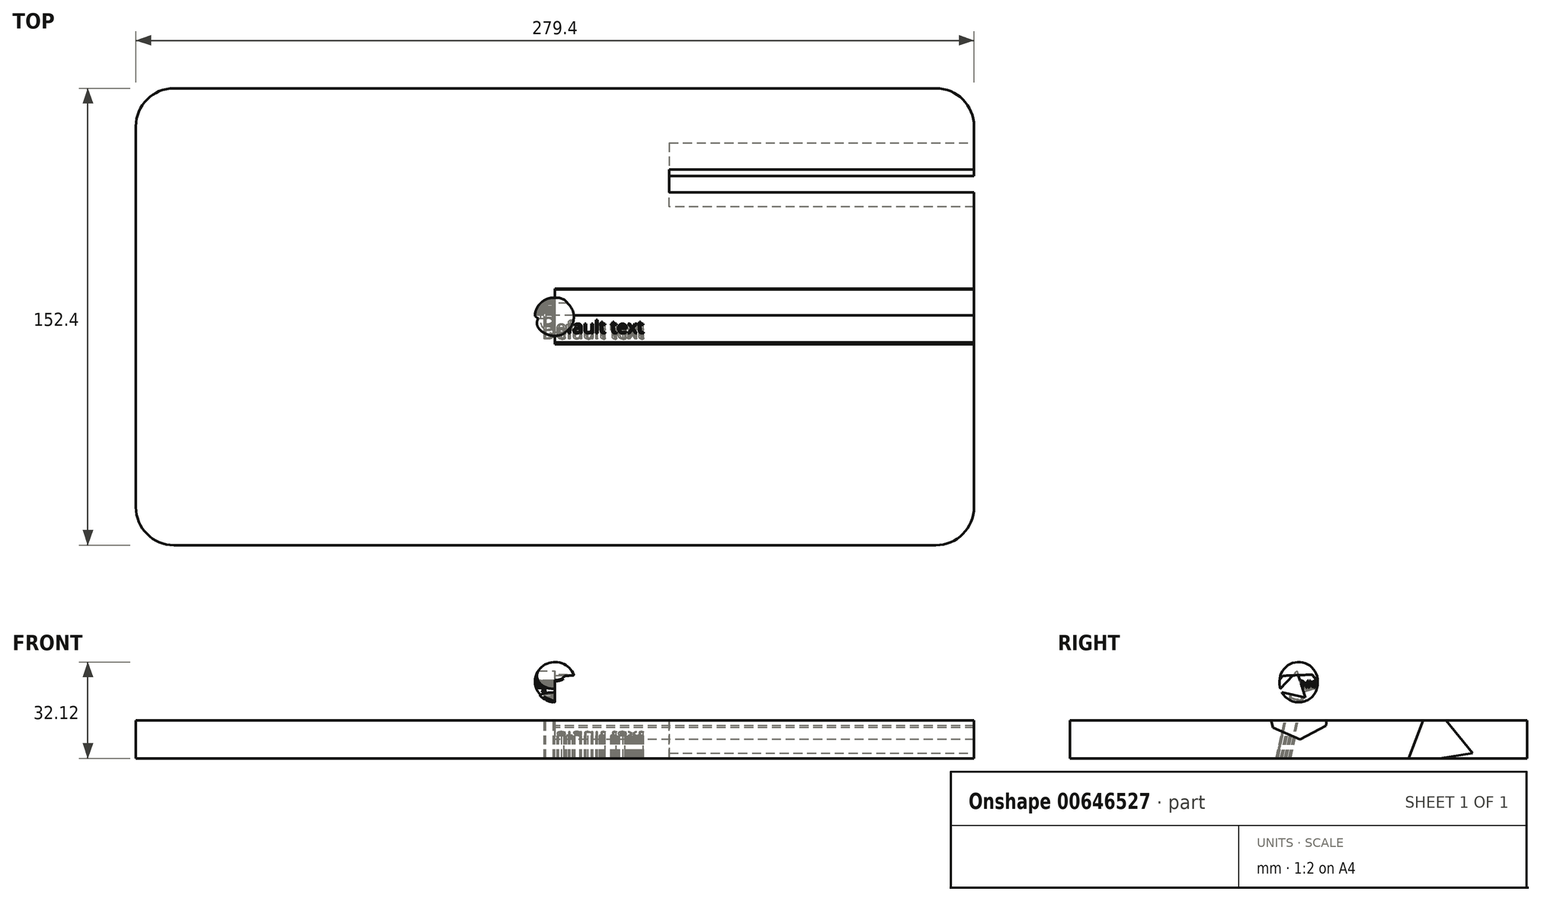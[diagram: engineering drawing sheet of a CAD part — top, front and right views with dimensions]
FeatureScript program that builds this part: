
annotation { "Feature Type Name" : "Feature", "Feature Type Description" : "" }
export const myFeature = defineFeature(function(context is Context, id is Id, definition is map)
    precondition{}
    {
        {
            var Q0;
            Q0=qCreatedBy(makeId("Top.planeOp"),FACE);
            var sketch = newSketch(context, id + "F0", { "sketchPlane" : qUnion([Q0])});
            skLineSegment(sketch, "E0.bottom", {"start": v(139.7, 76.2) * mm, "end": v(-139.7, 76.2) * mm});
            skLineSegment(sketch, "E0.top", {"start": v(139.7, -76.2) * mm, "end": v(-139.7, -76.2) * mm});
            skLineSegment(sketch, "E0.left", {"start": v(139.7, 76.2) * mm, "end": v(139.7, -76.2) * mm});
            skLineSegment(sketch, "E0.right", {"start": v(-139.7, 76.2) * mm, "end": v(-139.7, -76.2) * mm});
            skPoint(sketch, "E0.middle", {"position": v(0, 0) * mm});
            skSolve(sketch);
        }
        {
            var Q0;
            Q0=makeQuery(id+"F0.imprint","IMPRINT",FACE,{"disambiguationData":[TD([[makeQuery(id+"F0.imprint","IMPRINT",EDGE,{"derivedFrom":sQuery(id+"F0.wireOp",EDGE,"E0.bottom")}),1.0]])]});
            extrude(context, id + "F1", {"entities" : qUnion([Q0]), "endBound" : BoundingType.SYMMETRIC, "depth" : 12.7 * mm, "offsetDistance" : 25.4 * mm});
        }
        {
            var Q0;
            Q0=makeQuery(id+"F1.opExtrude","SWEPT_EDGE",EDGE,{"disambiguationData":[OSD([sQuery(id+"F0.wireOp",EDGE,"E0.top"),sQuery(id+"F0.wireOp",EDGE,"E0.right")])]});
            var Q1;
            Q1=makeQuery(id+"F1.opExtrude","SWEPT_EDGE",EDGE,{"disambiguationData":[OSD([sQuery(id+"F0.wireOp",EDGE,"E0.bottom"),sQuery(id+"F0.wireOp",EDGE,"E0.right")])]});
            var Q2;
            Q2=makeQuery(id+"F1.opExtrude","SWEPT_EDGE",EDGE,{"disambiguationData":[OSD([sQuery(id+"F0.wireOp",EDGE,"E0.bottom"),sQuery(id+"F0.wireOp",EDGE,"E0.left")])]});
            var Q3;
            Q3=makeQuery(id+"F1.opExtrude","SWEPT_EDGE",EDGE,{"disambiguationData":[OSD([sQuery(id+"F0.wireOp",EDGE,"E0.top"),sQuery(id+"F0.wireOp",EDGE,"E0.left")])]});
            fillet(context, id + "F2", {"entities" : qUnion([Q0, Q1, Q2, Q3]), "radius" : 12.7 * mm, "tangentPropagation" : true, "allowEdgeOverflow" : false});
        }
        {
            var Q0;
            Q0=makeQuery(id+"F1.opExtrude","CAP_FACE",FACE,{"disambiguationData":[OSD([sQuery(id+"F0.wireOp",EDGE,"E0.bottom"),sQuery(id+"F0.wireOp",EDGE,"E0.top"),sQuery(id+"F0.wireOp",EDGE,"E0.left"),sQuery(id+"F0.wireOp",EDGE,"E0.right")])],"isStart":false});
            var sketch = newSketch(context, id + "F3", { "sketchPlane" : qUnion([Q0])});
            skLineSegment(sketch, "E1", {"start": v(0, 76.2) * mm, "end": v(0, -76.2) * mm, "construction": true});
            skLineSegment(sketch, "E2", {"start": v(-139.7, 0) * mm, "end": v(139.7, 0) * mm, "construction": true});
            skPoint(sketch, "E3", {"position": v(0, 6.35) * mm});
            skPoint(sketch, "E4", {"position": v(0, -6.35) * mm});
            skArc(sketch, "E5", {"start": v(0, -6.35) * mm, "mid": v(6.72, 0) * mm, "end": v(0, 6.35) * mm});
            skLineSegment(sketch, "E6", {"start": v(0, 6.35) * mm, "end": v(0, -6.35) * mm});
            skSolve(sketch);
        }
        {
            var Q0;
            Q0=makeQuery(id+"F3.imprint","IMPRINT",FACE,{"disambiguationData":[TD([[makeQuery(id+"F3.imprint","IMPRINT",EDGE,{"derivedFrom":sQuery(id+"F3.wireOp",EDGE,"E5")}),1.0]])]});
            extrude(context, id + "F4", {"entities" : qUnion([Q0]), "operationType" : NewBodyOperationType.ADD, "depth" : 12.7 * mm, "offsetDistance" : 25.4 * mm});
        }
        {
            var Q0;
            Q0=makeQuery(id+"F4.opExtrude","CAP_FACE",FACE,{"disambiguationData":[OSD([sQuery(id+"F3.wireOp",EDGE,"E5"),sQuery(id+"F3.wireOp",EDGE,"E6")])],"isStart":false});
            var Q1;
            Q1=makeQuery(id+"F4.opExtrude","CAP_EDGE",EDGE,{"disambiguationData":[OSD([sQuery(id+"F3.wireOp",EDGE,"E6")])],"isStart":false});
            revolve(context, id + "F5", {"operationType" : NewBodyOperationType.ADD, "entities" : qUnion([Q0]), "axis" : qUnion([Q1]), "revolveType" : RevolveType.FULL});
        }
        {
            var Q0;
            Q0=makeQuery(id+"F4.opExtrude","SWEPT_FACE",FACE,{"disambiguationData":[OSD([sQuery(id+"F3.wireOp",EDGE,"E6")])]});
            var sketch = newSketch(context, id + "F6", { "sketchPlane" : qUnion([Q0])});
            skCircle(sketch, "E7.cCircle", {"center": v(0, 11.24) * mm, "radius": 10.14 * mm, "construction": true});
            skLineSegment(sketch, "E7.0", {"start": v(11.07, 13.3) * mm, "end": v(8.51, 3.87) * mm});
            skLineSegment(sketch, "E7.1", {"start": v(8.51, 3.87) * mm, "end": v(-0.45, -0.01) * mm});
            skLineSegment(sketch, "E7.2", {"start": v(-0.45, -0.01) * mm, "end": v(-9.08, 4.57) * mm});
            skLineSegment(sketch, "E7.3", {"start": v(-9.08, 4.57) * mm, "end": v(-10.87, 14.18) * mm});
            skLineSegment(sketch, "E7.4", {"start": v(-10.87, 14.18) * mm, "end": v(-4.48, 21.57) * mm});
            skLineSegment(sketch, "E7.5", {"start": v(-4.48, 21.57) * mm, "end": v(5.29, 21.18) * mm});
            skLineSegment(sketch, "E7.6", {"start": v(5.29, 21.18) * mm, "end": v(11.07, 13.3) * mm});
            skPoint(sketch, "E7.0.midPoint", {"position": v(9.8, 8.58) * mm});
            skSolve(sketch);
        }
        {
            var Q0;
            Q0=makeQuery(id+"F6.imprint","IMPRINT",FACE,{"disambiguationData":[TD([[makeQuery(id+"F6.imprint","IMPRINT",EDGE,{"derivedFrom":sQuery(id+"F6.wireOp",EDGE,"E7.0")}),-1.0]])]});
            var Q1;
            Q1 = qSketchRegion(id + "F6", true);
            extrude(context, id + "F7", {"entities" : qUnion([Q0, Q1]), "operationType" : NewBodyOperationType.REMOVE, "endBound" : BoundingType.THROUGH_ALL, "oppositeDirection" : true, "depth" : 25.4 * mm, "offsetDistance" : 25.4 * mm});
        }
        {
            var Q0;
            {var subQ0=sQuery(id+"F6.wireOp",EDGE,"E7.4");var subQ1=sQuery(id+"F6.wireOp",EDGE,"E7.5");var subQ2=sQuery(id+"F6.wireOp",EDGE,"E7.6");Q0=makeQuery(id+"F7.boolean.opBoolean","COPY",FACE,{"disambiguationData":[TD([makeQuery(id+"F5.opRevolve","SWEPT_FACE",FACE,{"disambiguationData":[OSD([sQuery(id+"F3.wireOp",EDGE,"E5")])]})])],"derivedFrom":makeQuery(id+"F7.opExtrude","CAP_FACE",FACE,{"disambiguationData":[OSD([sQuery(id+"F6.wireOp",EDGE,"E7.0"),sQuery(id+"F6.wireOp",EDGE,"E7.1"),sQuery(id+"F6.wireOp",EDGE,"E7.2"),sQuery(id+"F6.wireOp",EDGE,"E7.3"),subQ0,subQ1,subQ2])],"isStart":true})});}
            var sketch = newSketch(context, id + "F8", { "sketchPlane" : qUnion([Q0])});
            skCircle(sketch, "E8.cCircle", {"center": v(-1.7, 17.55) * mm, "radius": 2.7 * mm, "construction": true});
            skLineSegment(sketch, "E8.0", {"start": v(-0.55, 22.82) * mm, "end": v(2.27, 13.91) * mm});
            skLineSegment(sketch, "E8.1", {"start": v(2.27, 13.91) * mm, "end": v(-6.85, 15.92) * mm});
            skLineSegment(sketch, "E8.2", {"start": v(-6.85, 15.92) * mm, "end": v(-0.55, 22.82) * mm});
            skPoint(sketch, "E8.0.midPoint", {"position": v(0.86, 18.36) * mm});
            skSolve(sketch);
        }
        {
            var Q0;
            Q0 = qSketchRegion(id + "F8", true);
            extrude(context, id + "F9", {"entities" : qUnion([Q0]), "operationType" : NewBodyOperationType.REMOVE, "oppositeDirection" : true, "depth" : 25.4 * mm, "offsetDistance" : 25.4 * mm});
        }
        {
            var Q0;
            Q0=makeQuery(id+"F9.boolean.opBoolean","COPY",FACE,{"derivedFrom":makeQuery(id+"F9.opExtrude","SWEPT_FACE",FACE,{"disambiguationData":[OSD([sQuery(id+"F8.wireOp",EDGE,"E8.0")])]})});
            var sketch = newSketch(context, id + "F10", { "sketchPlane" : qUnion([Q0])});
            skText(sketch, "E9", { "text": "A", "fontName": "OpenSans-Regular.ttf"});
            const initialGuessF10  = {"E9": [-0.00433, 0.01448, 1, 0, 0.00147]};
            skSetInitialGuess(sketch, initialGuessF10);
            skSolve(sketch);
        }
        {
            var Q0;
            Q0 = qSketchRegion(id + "F10", true);
            extrude(context, id + "F11", {"entities" : qUnion([Q0]), "operationType" : NewBodyOperationType.REMOVE, "endBound" : BoundingType.THROUGH_ALL, "oppositeDirection" : true, "depth" : 25.4 * mm, "offsetDistance" : 25.4 * mm});
        }
        {
            var Q0;
            {var subQ1=sQuery(id+"F6.wireOp",EDGE,"E7.4");var subQ2=makeQuery(id+"F7.opExtrude","SWEPT_FACE",FACE,{"disambiguationData":[OSD([subQ1])]});var subQ4=sQuery(id+"F6.wireOp",EDGE,"E7.5");var subQ6=makeQuery(id+"F5.opRevolve","SWEPT_FACE",FACE,{"disambiguationData":[OSD([sQuery(id+"F3.wireOp",EDGE,"E5")])]});var subQ7=sQuery(id+"F6.wireOp",EDGE,"E7.6");Q0=makeQuery(id+"F9.boolean.opBoolean","SPLIT",FACE,{"disambiguationData":[TD([makeQuery(id+"F7.boolean.opBoolean","COPY",FACE,{"derivedFrom":subQ2})])],"derivedFrom":makeQuery(id+"F7.boolean.opBoolean","COPY",FACE,{"disambiguationData":[TD([subQ6])],"derivedFrom":makeQuery(id+"F7.opExtrude","CAP_FACE",FACE,{"disambiguationData":[OSD([sQuery(id+"F6.wireOp",EDGE,"E7.0"),sQuery(id+"F6.wireOp",EDGE,"E7.1"),sQuery(id+"F6.wireOp",EDGE,"E7.2"),sQuery(id+"F6.wireOp",EDGE,"E7.3"),subQ1,subQ4,subQ7])],"isStart":true})})});}
            var sketch = newSketch(context, id + "F12", { "sketchPlane" : qUnion([Q0])});
            skText(sketch, "E10", { "text": "@#$%", "fontName": "OpenSans-Regular.ttf"});
            const initialGuessF12  = {"E10": [-0.00075, 0.01726, 1, 0, 0.00235]};
            skSetInitialGuess(sketch, initialGuessF12);
            skSolve(sketch);
        }
        {
            var Q0;
            Q0 = qSketchRegion(id + "F12", true);
            extrude(context, id + "F13", {"entities" : qUnion([Q0]), "operationType" : NewBodyOperationType.REMOVE, "endBound" : BoundingType.THROUGH_ALL, "oppositeDirection" : true, "depth" : 25.4 * mm, "offsetDistance" : 25.4 * mm});
        }
        {
            var Q0;
            Q0=makeQuery(id+"F9.boolean.opBoolean","COPY",FACE,{"derivedFrom":makeQuery(id+"F9.opExtrude","SWEPT_FACE",FACE,{"disambiguationData":[OSD([sQuery(id+"F8.wireOp",EDGE,"E8.1")])]})});
            var sketch = newSketch(context, id + "F14", { "sketchPlane" : qUnion([Q0])});
            skText(sketch, "E11", { "text": "Default text", "fontName": "OpenSans-Regular.ttf"});
            const initialGuessF14  = {"E11": [-0.00417, -0.0059, 1, 0, 0.00446]};
            skSetInitialGuess(sketch, initialGuessF14);
            skSolve(sketch);
        }
        {
            var Q0;
            Q0 = qSketchRegion(id + "F14", true);
            extrude(context, id + "F15", {"entities" : qUnion([Q0]), "operationType" : NewBodyOperationType.REMOVE, "endBound" : BoundingType.THROUGH_ALL, "oppositeDirection" : true, "depth" : 25.4 * mm, "offsetDistance" : 25.4 * mm});
        }
        {
            var Q0;
            Q0=makeQuery(id+"F1.opExtrude","SWEPT_FACE",FACE,{"disambiguationData":[OSD([sQuery(id+"F0.wireOp",EDGE,"E0.left")])]});
            var sketch = newSketch(context, id + "F16", { "sketchPlane" : qUnion([Q0])});
            skCircle(sketch, "E12.cCircle", {"center": v(45.98, 0) * mm, "radius": 6.43 * mm, "construction": true});
            skLineSegment(sketch, "E12.0", {"start": v(58, -4.6) * mm, "end": v(36, -8.1) * mm});
            skLineSegment(sketch, "E12.1", {"start": v(36, -8.1) * mm, "end": v(43.95, 12.7) * mm});
            skLineSegment(sketch, "E12.2", {"start": v(43.95, 12.7) * mm, "end": v(58, -4.6) * mm});
            skPoint(sketch, "E12.0.midPoint", {"position": v(47, -6.35) * mm});
            skSolve(sketch);
        }
        {
            var Q0;
            Q0 = qSketchRegion(id + "F16", true);
            extrude(context, id + "F17", {"entities" : qUnion([Q0]), "operationType" : NewBodyOperationType.REMOVE, "oppositeDirection" : true, "depth" : 101.6 * mm, "offsetDistance" : 25.4 * mm});
        }
    });
